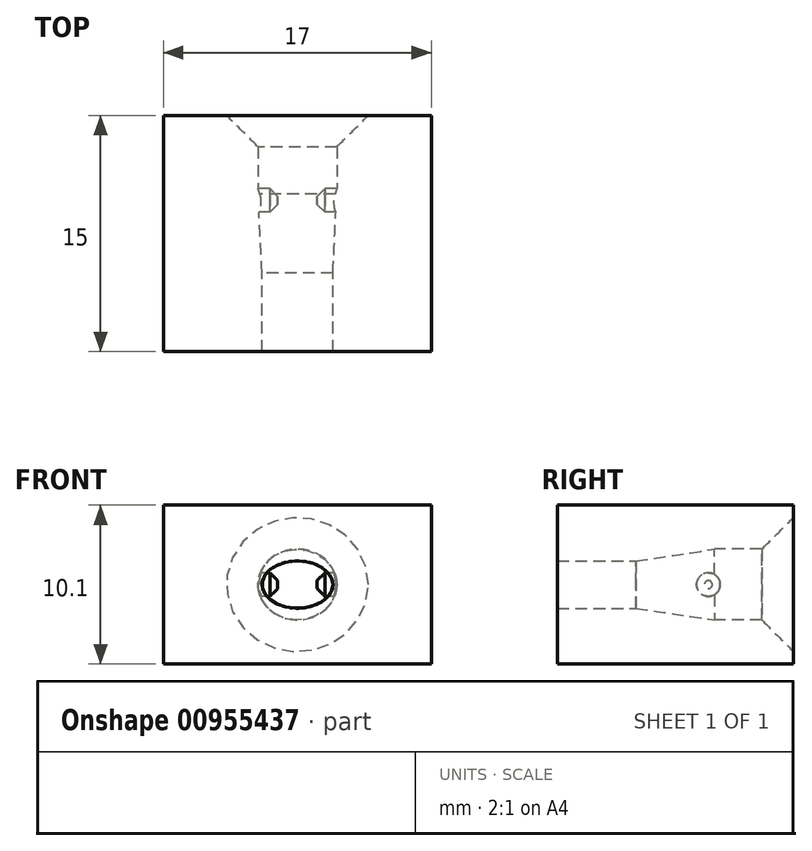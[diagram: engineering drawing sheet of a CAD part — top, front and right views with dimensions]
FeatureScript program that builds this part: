
annotation { "Feature Type Name" : "Feature", "Feature Type Description" : "" }
export const myFeature = defineFeature(function(context is Context, id is Id, definition is map)
    precondition{}
    {
        {
            var Q0;
            Q0=qCreatedBy(makeId("Front.planeOp"),FACE);
            var sketch = newSketch(context, id + "F0", { "sketchPlane" : qUnion([Q0])});
            skEllipse(sketch, "E0", {"center": v(0, 0) * mm, "majorRadius": 2.5 * mm, "minorRadius": 2.25 * mm, "majorAxis": v(1, 0)});
            skCircle(sketch, "E1", {"center": v(0, 0) * mm, "radius": 5 * mm});
            skSolve(sketch);
        }
        {
            var Q0;
            Q0=qCreatedBy(makeId("Front.planeOp"),FACE);
            cPlane(context, id + "F1", {"entities" : qUnion([Q0]), "cplaneType" : CPlaneType.OFFSET, "offset" : 5 * mm, "width" : 150 * mm, "height" : 150 * mm});
        }
        {
            var Q0;
            Q0=qCreatedBy(id+"F1.planeOp",FACE);
            var sketch = newSketch(context, id + "F2", { "sketchPlane" : qUnion([Q0])});
            skEllipse(sketch, "E2", {"center": v(0, 0) * mm, "majorRadius": 2.25 * mm, "minorRadius": 1.5 * mm, "majorAxis": v(1, 0)});
            skCircle(sketch, "E3", {"center": v(0, 0) * mm, "radius": 5 * mm});
            skSolve(sketch);
        }
        {
            var Q0;
            Q0=makeQuery(id+"F0.imprint","IMPRINT",FACE,{"disambiguationData":[TD([[makeQuery(id+"F0.imprint","IMPRINT",EDGE,{"derivedFrom":sQuery(id+"F0.wireOp",EDGE,"E0")}),-1.0]])]});
            var Q1;
            Q1=makeQuery(id+"F0.imprint","IMPRINT",FACE,{"disambiguationData":[TD([[makeQuery(id+"F0.imprint","IMPRINT",EDGE,{"derivedFrom":sQuery(id+"F0.wireOp",EDGE,"E0")}),1.0]])]});
            extrude(context, id + "F3", {"entities" : qUnion([Q0, Q1]), "depth" : 5 * mm, "offsetDistance" : 25 * mm});
        }
        {
            var Q1;
            Q1=makeQuery(id+"F2.imprint","IMPRINT",FACE,{"disambiguationData":[TD([[makeQuery(id+"F2.imprint","IMPRINT",EDGE,{"derivedFrom":sQuery(id+"F2.wireOp",EDGE,"E2")}),1.0]])]});
            var Q2;
            Q2=makeQuery(id+"F0.imprint","IMPRINT",FACE,{"disambiguationData":[TD([[makeQuery(id+"F0.imprint","IMPRINT",EDGE,{"derivedFrom":sQuery(id+"F0.wireOp",EDGE,"E0")}),1.0]])]});
            loft(context, id + "F4", {"operationType" : NewBodyOperationType.REMOVE, "sheetProfilesArray" : [{ "sheetProfileEntities" : qUnion([Q1]) }, { "sheetProfileEntities" : qUnion([Q2]) }]});
        }
        {
            var Q0;
            Q0=makeQuery(id+"F3.opExtrude","CAP_FACE",FACE,{"disambiguationData":[OSD([sQuery(id+"F0.wireOp",EDGE,"E1")])],"isStart":false});
            var sketch = newSketch(context, id + "F5", { "sketchPlane" : qUnion([Q0])});
            skCircle(sketch, "E4", {"center": v(0, 0) * mm, "radius": 5 * mm});
            skSolve(sketch);
        }
        {
            var Q0;
            Q0=makeQuery(id+"F5.imprint","IMPRINT",FACE,{"disambiguationData":[TD([[makeQuery(id+"F5.imprint","IMPRINT",EDGE,{"derivedFrom":sQuery(id+"F5.wireOp",EDGE,"E4")}),1.0]])]});
            var Q1;
            Q1=makeQuery(id+"F5.imprint","IMPRINT",FACE,{"disambiguationData":[TD([[makeQuery(id+"F5.imprint","IMPRINT",EDGE,{"derivedFrom":makeQuery(id+"F4.boolean.opBoolean","COPY",EDGE,{"derivedFrom":makeQuery(id+"F4.opLoft","MID_CAP_EDGE",EDGE,{"disambiguationData":[OSD([sQuery(id+"F2.wireOp",EDGE,"E2")])],"capPos":0.0})})}),-1.0]])]});
            extrude(context, id + "F6", {"entities" : qUnion([Q0, Q1]), "operationType" : NewBodyOperationType.ADD, "depth" : 5 * mm, "offsetDistance" : 25 * mm});
        }
        {
            var Q0;
            Q0=makeQuery(id+"F0.imprint","IMPRINT",FACE,{"disambiguationData":[TD([[makeQuery(id+"F0.imprint","IMPRINT",EDGE,{"derivedFrom":sQuery(id+"F0.wireOp",EDGE,"E0")}),-1.0]])]});
            extrude(context, id + "F7", {"entities" : qUnion([Q0]), "operationType" : NewBodyOperationType.ADD, "oppositeDirection" : true, "depth" : 5 * mm, "offsetDistance" : 25 * mm});
        }
        {
            var Q0;
            Q0=makeQuery(id+"F7.opExtrude","CAP_EDGE",EDGE,{"disambiguationData":[OSD([sQuery(id+"F0.wireOp",EDGE,"E0")])],"isStart":false});
            chamfer(context, id + "F8", {"entities" : qUnion([Q0]), "width" : 2 * mm, "tangentPropagation" : true});
        }
        {
            var Q0;
            Q0=qCreatedBy(makeId("Right.planeOp"),FACE);
            var sketch = newSketch(context, id + "F9", { "sketchPlane" : qUnion([Q0])});
            skCircle(sketch, "E5", {"center": v(-0.4, 0) * mm, "radius": 0.75 * mm});
            skSolve(sketch);
        }
        {
            var Q0;
            Q0 = qSketchRegion(id + "F9", true);
            extrude(context, id + "F10", {"entities" : qUnion([Q0]), "operationType" : NewBodyOperationType.ADD, "depth" : 4.5 * mm, "offsetDistance" : 25 * mm, "hasSecondDirection" : true, "secondDirectionOppositeDirection" : true, "secondDirectionDepth" : 4.5 * mm});
        }
        {
            var Q0;
            Q0=qCreatedBy(makeId("Front.planeOp"),FACE);
            var sketch = newSketch(context, id + "F11", { "sketchPlane" : qUnion([Q0])});
            skLineSegment(sketch, "E6.bottom", {"start": v(-1.25, 0.75) * mm, "end": v(1.25, 0.75) * mm});
            skLineSegment(sketch, "E6.top", {"start": v(-1.25, -0.75) * mm, "end": v(1.25, -0.75) * mm});
            skLineSegment(sketch, "E6.left", {"start": v(-1.25, 0.75) * mm, "end": v(-1.25, -0.75) * mm});
            skLineSegment(sketch, "E6.right", {"start": v(1.25, 0.75) * mm, "end": v(1.25, -0.75) * mm});
            skPoint(sketch, "E6.middle", {"position": v(0, 0) * mm});
            skSolve(sketch);
        }
        {
            var Q0;
            Q0=makeQuery(id+"F11.imprint","IMPRINT",FACE,{"disambiguationData":[TD([[makeQuery(id+"F11.imprint","IMPRINT",EDGE,{"derivedFrom":sQuery(id+"F11.wireOp",EDGE,"E6.bottom")}),-1.0]])]});
            extrude(context, id + "F12", {"entities" : qUnion([Q0]), "operationType" : NewBodyOperationType.REMOVE, "depth" : 2 * mm, "offsetDistance" : 25 * mm, "hasSecondDirection" : true, "secondDirectionOppositeDirection" : true, "secondDirectionDepth" : 2 * mm});
        }
        {
            var Q0;
            Q0=makeQuery(id+"F12.boolean.opBoolean","INTERSECT",EDGE,{"derivedFrom":[makeQuery(id+"F10.opExtrude","SWEPT_FACE",FACE,{"disambiguationData":[OSD([sQuery(id+"F9.wireOp",EDGE,"E5")])]}),makeQuery(id+"F12.opExtrude","SWEPT_FACE",FACE,{"disambiguationData":[OSD([sQuery(id+"F11.wireOp",EDGE,"E6.right")])]})]});
            var Q1;
            Q1=makeQuery(id+"F12.boolean.opBoolean","INTERSECT",EDGE,{"derivedFrom":[makeQuery(id+"F10.opExtrude","SWEPT_FACE",FACE,{"disambiguationData":[OSD([sQuery(id+"F9.wireOp",EDGE,"E5")])]}),makeQuery(id+"F12.opExtrude","SWEPT_FACE",FACE,{"disambiguationData":[OSD([sQuery(id+"F11.wireOp",EDGE,"E6.left")])]})]});
            chamfer(context, id + "F13", {"entities" : qUnion([Q0, Q1]), "width" : 0.5 * mm, "tangentPropagation" : true});
        }
        {
            var Q0;
            Q0=makeQuery(id+"F6.opExtrude","CAP_FACE",FACE,{"disambiguationData":[OSD([sQuery(id+"F5.wireOp",EDGE,"E4")])],"isStart":false});
            var sketch = newSketch(context, id + "F14", { "sketchPlane" : qUnion([Q0])});
            skLineSegment(sketch, "E7.bottom", {"start": v(8.5, 5.05) * mm, "end": v(-8.5, 5.05) * mm});
            skLineSegment(sketch, "E7.top", {"start": v(8.5, -5.05) * mm, "end": v(-8.5, -5.05) * mm});
            skLineSegment(sketch, "E7.left", {"start": v(8.5, 5.05) * mm, "end": v(8.5, -5.05) * mm});
            skLineSegment(sketch, "E7.right", {"start": v(-8.5, 5.05) * mm, "end": v(-8.5, -5.05) * mm});
            skPoint(sketch, "E7.middle", {"position": v(0, 0) * mm});
            skSolve(sketch);
        }
        {
            var Q0;
            {var subQ0=sQuery(id+"F14.wireOp",EDGE,"E7.left");Q0=makeQuery(id+"F14.imprint","IMPRINT",FACE,{"disambiguationData":[TD([[makeQuery(id+"F14.imprint","IMPRINT",EDGE,{"derivedFrom":subQ0}),-1.0]])]});}
            var Q1;
            {var subQ0=sQuery(id+"F14.wireOp",EDGE,"E7.right");Q1=makeQuery(id+"F14.imprint","IMPRINT",FACE,{"disambiguationData":[TD([[makeQuery(id+"F14.imprint","IMPRINT",EDGE,{"derivedFrom":subQ0}),1.0]])]});}
            extrude(context, id + "F15", {"entities" : qUnion([Q0, Q1]), "operationType" : NewBodyOperationType.ADD, "oppositeDirection" : true, "depth" : 15 * mm, "offsetDistance" : 25 * mm});
        }
    });
